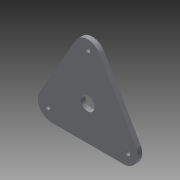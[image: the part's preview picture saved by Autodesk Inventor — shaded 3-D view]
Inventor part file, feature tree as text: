
AUTODESK INVENTOR PART (.ipt)
format: ipt  version: 2013 (Build 170138000, 138)  size: 94,208 bytes
history: native  units: in
note: dims shown in document units (in); Inventor stores cm internally (conversion verified against a paired STEP export)
features: extrude x1, fillet x1, sketch x1
ambient origin geometry x8: Origin, YZ Plane, XZ Plane, XY Plane, X Axis, Y Axis, Z Axis, Center Point
bodies: Solid1 (feature_tree)
feature tree (3):
  extrude  "Extrusion1"  Depth=0.25in
  fillet  "Fillet1"  Radius=2.5in
  sketch  "Sketch2"  dims[d0=0.75in d1=0.25in d2=2.5in d3=1.1811in d5=360.0deg d8=0.5in d9=0.5in d10=0.5in d11=0.25in d12=0.0in d13=0.75in]
